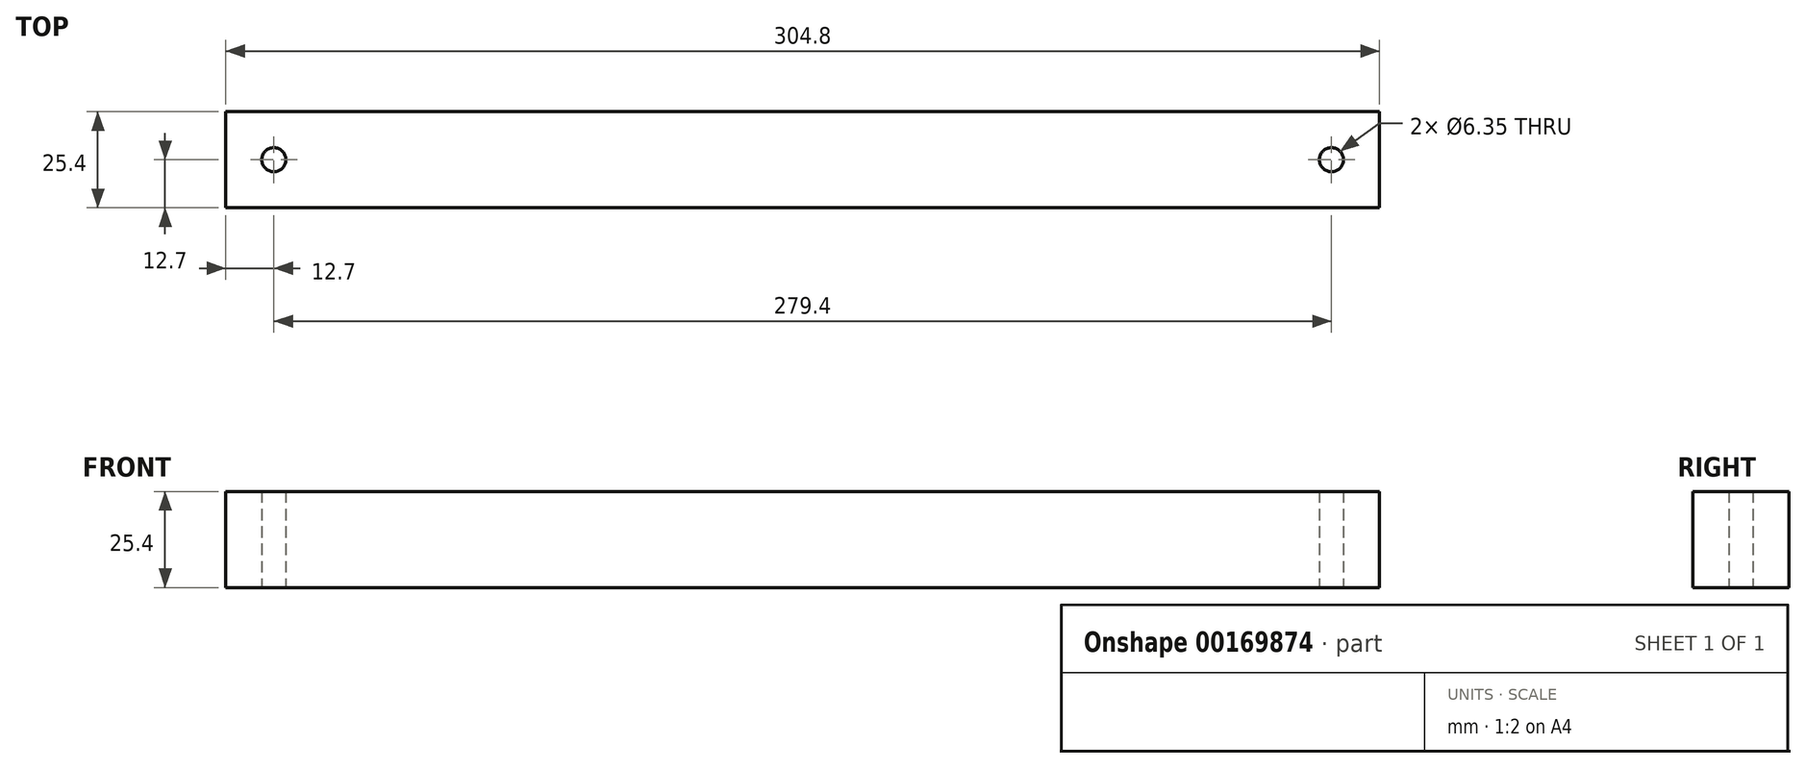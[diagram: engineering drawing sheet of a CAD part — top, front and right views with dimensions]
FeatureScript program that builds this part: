
annotation { "Feature Type Name" : "Feature", "Feature Type Description" : "" }
export const myFeature = defineFeature(function(context is Context, id is Id, definition is map)
    precondition{}
    {
        {
            var Q0;
            Q0=qCreatedBy(makeId("Top.planeOp"),FACE);
            var sketch = newSketch(context, id + "F0", { "sketchPlane" : qUnion([Q0])});
            skLineSegment(sketch, "E0.bottom", {"start": v(0, 0) * mm, "end": v(-304.8, 0) * mm});
            skLineSegment(sketch, "E0.top", {"start": v(0, 25.4) * mm, "end": v(-304.8, 25.4) * mm});
            skLineSegment(sketch, "E0.left", {"start": v(0, 0) * mm, "end": v(0, 25.4) * mm});
            skLineSegment(sketch, "E0.right", {"start": v(-304.8, 0) * mm, "end": v(-304.8, 25.4) * mm});
            skLineSegment(sketch, "E1", {"start": v(-304.8, 12.7) * mm, "end": v(0, 12.7) * mm, "construction": true});
            skLineSegment(sketch, "E2", {"start": v(-152.4, 12.7) * mm, "end": v(-152.4, 25.4) * mm, "construction": true});
            skCircle(sketch, "E3", {"center": v(-292.1, 12.7) * mm, "radius": 3.18 * mm});
            skCircle(sketch, "E4.MirrorC", {"center": v(-12.7, 12.7) * mm, "radius": 3.18 * mm});
            skSolve(sketch);
        }
        {
            var Q0;
            Q0 = qSketchRegion(id + "F0", true);
            extrude(context, id + "F1", {"entities" : qUnion([Q0]), "depth" : 25.4 * mm});
        }
    });
